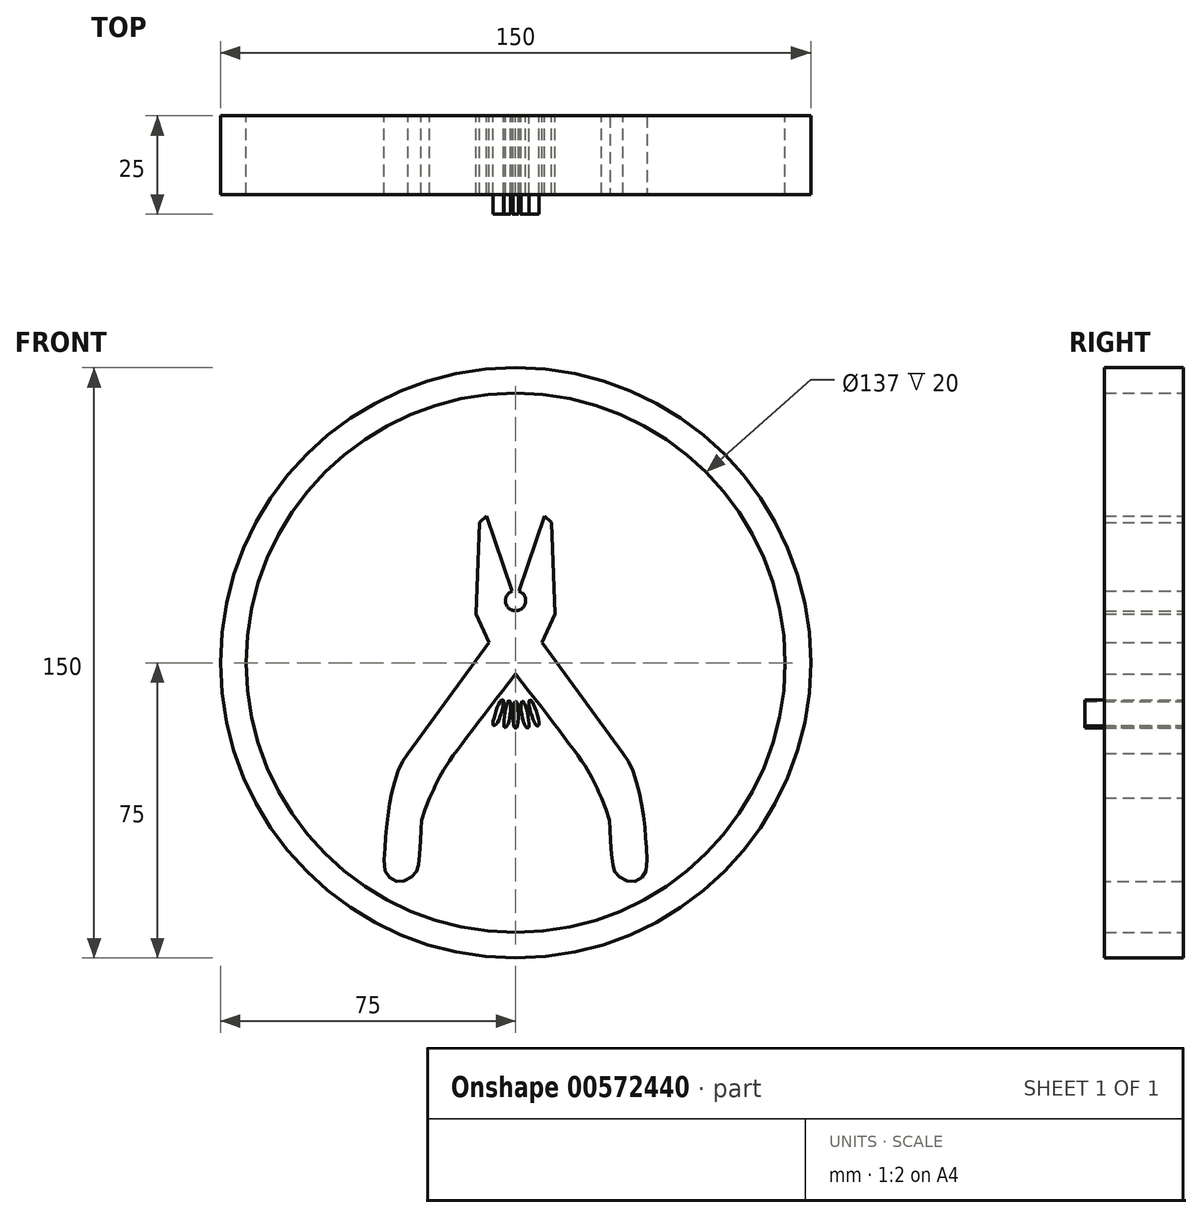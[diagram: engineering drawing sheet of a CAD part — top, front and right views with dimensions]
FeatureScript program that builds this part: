
annotation { "Feature Type Name" : "Feature", "Feature Type Description" : "" }
export const myFeature = defineFeature(function(context is Context, id is Id, definition is map)
    precondition{}
    {
        {
            var Q0;
            Q0=qCreatedBy(makeId("Front.planeOp"),FACE);
            var sketch = newSketch(context, id + "F0", { "sketchPlane" : qUnion([Q0])});
            skCircle(sketch, "E0", {"center": v(0, 0) * mm, "radius": 75 * mm});
            skCircle(sketch, "E1", {"center": v(0, 0) * mm, "radius": 68.5 * mm});
            skSolve(sketch);
        }
        {
            var Q0;
            Q0=qCreatedBy(makeId("Front.planeOp"),FACE);
            var sketch = newSketch(context, id + "F1", { "sketchPlane" : qUnion([Q0])});
            skLineSegment(sketch, "E2", {"start": v(-10, 12.39) * mm, "end": v(-9.1, 35.71) * mm});
            skLineSegment(sketch, "E3", {"start": v(-7.34, 37.33) * mm, "end": v(-9.1, 35.71) * mm});
            skLineSegment(sketch, "E4", {"start": v(-0.85, 18.26) * mm, "end": v(-7.34, 37.33) * mm});
            skLineSegment(sketch, "E5", {"start": v(0, -66.58) * mm, "end": v(0, 74.82) * mm});
            skLineSegment(sketch, "E6.MirrorCS", {"start": v(10, 12.39) * mm, "end": v(9.1, 35.71) * mm});
            skLineSegment(sketch, "E7.MirrorCS", {"start": v(7.34, 37.33) * mm, "end": v(9.1, 35.71) * mm});
            skLineSegment(sketch, "E8.MirrorCS", {"start": v(0.85, 18.26) * mm, "end": v(7.34, 37.33) * mm});
            skLineSegment(sketch, "E9", {"start": v(-6.7, 5.13) * mm, "end": v(-10, 12.39) * mm});
            skLineSegment(sketch, "E10", {"start": v(-6.7, 5.13) * mm, "end": v(-27.27, -22.98) * mm});
            skFitSpline(sketch, "E11", {"points": [v(-27.27, -22.98) * mm, v(-29.52, -26.66) * mm, v(-31.19, -31.98) * mm, v(-32.18, -37) * mm, v(-32.9, -42.7) * mm, v(-33.2, -47.05) * mm, v(-33.15, -52.71) * mm, v(-31.74, -54.8) * mm, v(-29.23, -55.6) * mm, v(-26.69, -54.58) * mm, v(-25.03, -52.76) * mm, v(-24.62, -50.5) * mm, v(-24.04, -43.94) * mm, v(-23.84, -39.86) * mm, v(-21.83, -34.33) * mm], "startDerivative": vector(-32.83, -46.76) * mm, "endDerivative": vector(25.22, 69.7) * mm});
            skFitSpline(sketch, "E12", {"points": [v(-21.83, -34.33) * mm, v(-20.19, -30.76) * mm, v(-17.28, -25.65) * mm, v(0, -2.87) * mm], "startDerivative": vector(9.4, 17.1) * mm, "endDerivative": vector(38.2, 48.97) * mm});
            skLineSegment(sketch, "E13.MirrorCS", {"start": v(6.7, 5.13) * mm, "end": v(27.27, -22.98) * mm});
            skFitSpline(sketch, "E14.MirrorCS", {"points": [v(27.27, -22.98) * mm, v(29.52, -26.66) * mm, v(31.19, -31.98) * mm, v(32.18, -37) * mm, v(32.9, -42.7) * mm, v(33.2, -47.05) * mm, v(33.15, -52.71) * mm, v(31.74, -54.8) * mm, v(29.23, -55.6) * mm, v(26.69, -54.58) * mm, v(25.03, -52.76) * mm, v(24.62, -50.5) * mm, v(24.04, -43.94) * mm, v(23.84, -39.86) * mm, v(21.83, -34.33) * mm], "startDerivative": vector(32.83, -46.76) * mm, "endDerivative": vector(-25.22, 69.7) * mm});
            skFitSpline(sketch, "E15.MirrorCS", {"points": [v(21.83, -34.33) * mm, v(20.19, -30.76) * mm, v(17.28, -25.65) * mm, v(0, -2.87) * mm], "startDerivative": vector(-9.4, 17.1) * mm, "endDerivative": vector(-38.2, 48.97) * mm});
            skLineSegment(sketch, "E16.MirrorCS", {"start": v(6.7, 5.13) * mm, "end": v(10, 12.39) * mm});
            skArc(sketch, "E17", {"start": v(-0.85, 18.26) * mm, "mid": v(0, 13.25) * mm, "end": v(0.85, 18.26) * mm});
            skSolve(sketch);
        }
        {
            var Q0;
            Q0=qCreatedBy(makeId("Front.planeOp"),FACE);
            var sketch = newSketch(context, id + "F2", { "sketchPlane" : qUnion([Q0])});
            skFitSpline(sketch, "E18", {"points": [v(-3.98, -9.96) * mm, v(-5.72, -15.04) * mm, v(-5.64, -15.82) * mm, v(-4.86, -15.53) * mm, v(-3.06, -10.2) * mm, v(-3.2, -9.44) * mm, v(-3.98, -9.96) * mm]});
            skFitSpline(sketch, "E19", {"points": [v(-2.14, -10.22) * mm, v(-2.96, -15.58) * mm, v(-2.8, -16.37) * mm, v(-2.1, -15.93) * mm, v(-1.26, -10.36) * mm, v(-1.56, -9.7) * mm, v(-2.14, -10.22) * mm]});
            skFitSpline(sketch, "E20", {"points": [v(-0.44, -10.44) * mm, v(-0.48, -15.9) * mm, v(0, -16.58) * mm, v(0.5, -15.94) * mm, v(0.44, -10.41) * mm, v(0, -9.83) * mm, v(-0.44, -10.44) * mm]});
            skFitSpline(sketch, "E21", {"points": [v(1.37, -10.63) * mm, v(2.36, -15.88) * mm, v(3.04, -16.5) * mm, v(3.4, -15.74) * mm, v(2.3, -10.35) * mm, v(1.75, -9.75) * mm, v(1.37, -10.63) * mm]});
            skFitSpline(sketch, "E22", {"points": [v(3.37, -10.2) * mm, v(4.87, -15.34) * mm, v(5.6, -16.02) * mm, v(5.92, -15.28) * mm, v(4.2, -9.9) * mm, v(3.57, -9.45) * mm, v(3.37, -10.2) * mm]});
            skFitSpline(sketch, "E23", {"points": [v(-13.47, -4.13) * mm, v(-16.08, -2.4) * mm, v(-17.3, -1.42) * mm, v(-20, -0.93) * mm, v(-21.37, -0.85) * mm, v(-21.77, -1.8) * mm, v(-21.82, -3.16) * mm, v(-21.65, -5.17) * mm, v(-21.56, -6.43) * mm, v(-21.68, -7.67) * mm, v(-21.77, -9.29) * mm, v(-21.96, -10.7) * mm, v(-22.66, -12.22) * mm, v(-23.33, -13.71) * mm, v(-24.22, -14) * mm, v(-25.5, -13.92) * mm, v(-27.2, -13.31) * mm, v(-28.1, -12.43) * mm, v(-29.04, -11.33) * mm, v(-30.5, -9.22) * mm, v(-30.99, -6.9) * mm, v(-31.16, -4.4) * mm, v(-31.16, -1.77) * mm, v(-31, 0.4) * mm], "startDerivative": vector(-48.66, 28.91) * mm, "endDerivative": vector(-3.44, 5.53) * mm});
            skFitSpline(sketch, "E24", {"points": [v(-31, 0.4) * mm, v(-30.88, 2.85) * mm, v(-30.32, 9) * mm, v(-29.28, 13.1) * mm, v(-26.86, 21.89) * mm, v(-24.96, 27.1) * mm, v(-22.12, 34.55) * mm, v(-19.6, 41) * mm, v(-17.58, 45.38) * mm, v(-15.62, 49.61) * mm, v(-14, 53.95) * mm, v(-14.22, 54.45) * mm, v(-14.94, 54.43) * mm, v(-16, 53.95) * mm, v(-17.36, 53.2) * mm, v(-18.07, 52.68) * mm, v(-18.67, 51.88) * mm, v(-19.18, 51.15) * mm, v(-19.32, 49.73) * mm, v(-19.55, 48.7) * mm, v(-19.8, 48.07) * mm, v(-20.3, 47.76) * mm, v(-20.59, 48.4) * mm, v(-20.92, 48.56) * mm, v(-21.2, 48.46) * mm, v(-21.37, 48.26) * mm, v(-21.53, 47.56) * mm, v(-21.99, 46.7) * mm, v(-22.33, 45) * mm, v(-22.33, 43.87) * mm, v(-22.28, 43.09) * mm, v(-22.72, 42.65) * mm, v(-23.3, 42.8) * mm, v(-23.45, 44.01) * mm, v(-23.74, 45) * mm, v(-24.48, 44.84) * mm, v(-24.66, 44.23) * mm, v(-25.07, 42.62) * mm, v(-25.6, 40.8) * mm, v(-25.74, 38.94) * mm, v(-25.42, 37) * mm, v(-25.02, 36.15) * mm, v(-25.23, 35.7) * mm, v(-25.98, 35.8) * mm, v(-26.35, 36.68) * mm, v(-26.59, 37.4) * mm, v(-26.72, 38.17) * mm, v(-26.8, 38.62) * mm, v(-26.83, 39.13) * mm, v(-27.33, 39.4) * mm, v(-27.9, 39.13) * mm, v(-28.1, 38.57) * mm, v(-28.61, 37.48) * mm, v(-28.9, 36.5) * mm, v(-29.28, 35.75) * mm, v(-29.52, 34.82) * mm, v(-29.96, 32.65) * mm, v(-29.8, 30.62) * mm, v(-29.29, 28.77) * mm, v(-29.83, 28.07) * mm, v(-30.87, 28.88) * mm, v(-31.49, 29.8) * mm, v(-32.2, 30.88) * mm, v(-32.48, 31.53) * mm, v(-32.96, 32.21) * mm, v(-33.07, 32.21) * mm, v(-33.22, 32.13) * mm, v(-33.4, 31.87) * mm, v(-33.92, 30.73) * mm, v(-33.95, 30.1) * mm, v(-34.05, 28.97) * mm, v(-34.11, 28.61) * mm, v(-34.05, 27.97) * mm, v(-34, 27.37) * mm, v(-34, 26.87) * mm, v(-33.95, 26.48) * mm, v(-33.85, 24.34) * mm, v(-33.58, 23.12) * mm, v(-33.12, 21.52) * mm, v(-32.86, 20.69) * mm, v(-32.66, 20.29) * mm, v(-32.82, 19.9) * mm, v(-33.4, 20.08) * mm, v(-34, 20.65) * mm, v(-34.76, 21.37) * mm, v(-35.55, 22.12) * mm, v(-36, 22.75) * mm, v(-36.45, 23.23) * mm, v(-36.86, 23.77) * mm, v(-37.3, 24.06) * mm, v(-37.56, 23.67) * mm, v(-37.68, 22.87) * mm, v(-37.66, 21.9) * mm, v(-37.72, 21.41) * mm, v(-37.68, 20.67) * mm, v(-37.64, 19.98) * mm, v(-37.62, 19.36) * mm, v(-37.62, 18.35) * mm, v(-37.62, 17.66) * mm, v(-37.56, 17.18) * mm, v(-37.56, 16.67) * mm, v(-37.4, 15.06) * mm, v(-36.94, 13.86) * mm, v(-36.32, 12.7) * mm, v(-35.62, 11.78) * mm, v(-34.9, 11.12) * mm, v(-34.83, 10.45) * mm, v(-35, 9.92) * mm, v(-35.58, 10.35) * mm, v(-38.88, 13.71) * mm, v(-40.64, 15.4) * mm, v(-41.72, 16.36) * mm, v(-41.98, 15.88) * mm, v(-41.88, 14.74) * mm, v(-41.79, 14) * mm, v(-41.69, 13.44) * mm, v(-41.62, 12.9) * mm, v(-41.55, 12.22) * mm, v(-41.3, 11.5) * mm, v(-41, 10.68) * mm, v(-40.65, 9.92) * mm, v(-40.33, 9.06) * mm, v(-40, 7.98) * mm, v(-39.44, 7.18) * mm, v(-38.62, 6.32) * mm, v(-39.13, 5.74) * mm, v(-40.38, 6.4) * mm, v(-41.58, 7.16) * mm, v(-43.16, 8.23) * mm, v(-45.26, 9.75) * mm, v(-45.7, 10.06) * mm, v(-46, 10.08) * mm, v(-46.3, 9.93) * mm, v(-46.4, 9.5) * mm, v(-46.3, 8.79) * mm, v(-46.28, 7.94) * mm, v(-46.06, 7.05) * mm, v(-45.57, 6.1) * mm, v(-44.97, 5.11) * mm, v(-43.87, 3.6) * mm, v(-42.7, 2.08) * mm, v(-41.65, 1.06) * mm, v(-41.12, 0.63) * mm, v(-40.92, 0.4) * mm, v(-41.2, 0.2) * mm, v(-42.06, 0.25) * mm, v(-42.78, 0.4) * mm, v(-43.47, 0.66) * mm, v(-44.3, 0.93) * mm, v(-45.62, 1.28) * mm, v(-46.58, 1.31) * mm, v(-46.78, 1.16) * mm, v(-46.83, 0.98) * mm, v(-46.83, 0.76) * mm, v(-46.63, -0.18) * mm, v(-46.13, -0.96) * mm, v(-45.62, -1.77) * mm, v(-45.12, -2.43) * mm, v(-44.59, -3) * mm, v(-43.61, -4.04) * mm, v(-42.82, -4.7) * mm, v(-42.4, -5) * mm, v(-42.2, -5.16) * mm, v(-42.12, -5.35) * mm, v(-42.34, -5.47) * mm, v(-42.85, -5.51) * mm, v(-44.87, -5.47) * mm, v(-46.1, -5.5) * mm, v(-47.24, -5.43) * mm, v(-47.54, -5.7) * mm, v(-47.52, -6.22) * mm, v(-47.09, -6.74) * mm, v(-46.59, -7.39) * mm, v(-46, -8.02) * mm, v(-45.2, -8.79) * mm, v(-44.62, -9.29) * mm, v(-44.05, -9.9) * mm, v(-43.24, -10.52) * mm, v(-42.54, -10.99) * mm, v(-41.6, -11.64) * mm, v(-40.78, -12.07) * mm, v(-39.95, -12.39) * mm, v(-38.98, -12.9) * mm, v(-38.42, -13.04) * mm, v(-38.42, -13.21) * mm, v(-38.55, -13.28) * mm, v(-39.17, -13.34) * mm, v(-40.6, -13.47) * mm, v(-41.67, -13.79) * mm, v(-42.3, -13.98) * mm, v(-43.1, -14.4) * mm, v(-43.87, -14.63) * mm, v(-44.51, -14.92) * mm, v(-44.54, -15.21) * mm, v(-44.25, -15.36) * mm, v(-43.78, -15.68) * mm, v(-42.87, -16.06) * mm, v(-41.26, -16.65) * mm, v(-39.53, -16.98) * mm, v(-37.63, -17.1) * mm, v(-35.74, -17.3) * mm, v(-34.13, -17.3) * mm, v(-33.04, -17.3) * mm, v(-32.82, -17.4) * mm, v(-32.9, -17.62) * mm, v(-33.19, -17.69) * mm, v(-33.96, -17.88) * mm, v(-34.89, -18.03) * mm, v(-36.08, -18.25) * mm, v(-36.78, -18.25) * mm, v(-37.83, -18.47) * mm, v(-38.77, -18.76) * mm, v(-40.11, -18.93) * mm, v(-41, -19.05) * mm, v(-42.15, -19.2) * mm, v(-42.9, -19.39) * mm, v(-43.05, -19.8) * mm, v(-42.88, -20.21) * mm, v(-42.54, -20.7) * mm, v(-41.81, -21.04) * mm, v(-41.1, -21.33) * mm, v(-39.94, -21.6) * mm, v(-38.8, -21.84) * mm, v(-37.68, -22.16) * mm, v(-36.44, -22.04) * mm, v(-35.37, -22.08) * mm, v(-33.8, -22.06) * mm, v(-32.94, -21.99) * mm, v(-31.73, -21.87) * mm, v(-30.54, -21.9) * mm, v(-29.42, -21.87) * mm, v(-28.55, -21.87) * mm, v(-27.99, -22.01) * mm, v(-27.56, -22.25) * mm, v(-27.35, -22.53) * mm, v(-27.53, -22.89) * mm, v(-27.78, -23.17) * mm, v(-28.1, -23.38) * mm, v(-28.58, -23.73) * mm, v(-29.4, -24.18) * mm, v(-30.22, -24.62) * mm, v(-30.87, -24.94) * mm, v(-31.37, -25.18) * mm, v(-31.85, -25.43) * mm, v(-31.92, -25.58) * mm, v(-31.82, -25.67) * mm, v(-31.64, -25.8) * mm, v(-31.36, -25.87) * mm, v(-31.16, -25.97) * mm, v(-30.33, -26.13) * mm, v(-29.84, -26.26) * mm, v(-29.54, -26.44) * mm, v(-29.4, -26.48) * mm, v(-29.4, -26.48) * mm], "startDerivative": vector(14.67, 321.67) * mm, "endDerivative": vector(0.41, 1.71) * mm});
            skFitSpline(sketch, "E25.MirrorCS", {"points": [v(31, 0.4) * mm, v(30.88, 2.85) * mm, v(30.32, 9) * mm, v(29.28, 13.1) * mm, v(26.86, 21.89) * mm, v(24.96, 27.1) * mm, v(22.12, 34.55) * mm, v(19.6, 41) * mm, v(17.58, 45.38) * mm, v(15.62, 49.61) * mm, v(14, 53.95) * mm, v(14.22, 54.45) * mm, v(14.94, 54.43) * mm, v(16, 53.95) * mm, v(17.36, 53.2) * mm, v(18.07, 52.68) * mm, v(18.67, 51.88) * mm, v(19.18, 51.15) * mm, v(19.32, 49.73) * mm, v(19.55, 48.7) * mm, v(19.8, 48.07) * mm, v(20.3, 47.76) * mm, v(20.59, 48.4) * mm, v(20.92, 48.56) * mm, v(21.2, 48.46) * mm, v(21.37, 48.26) * mm, v(21.53, 47.56) * mm, v(21.99, 46.7) * mm, v(22.33, 45) * mm, v(22.33, 43.87) * mm, v(22.28, 43.09) * mm, v(22.72, 42.65) * mm, v(23.3, 42.8) * mm, v(23.45, 44.01) * mm, v(23.74, 45) * mm, v(24.48, 44.84) * mm, v(24.66, 44.23) * mm, v(25.07, 42.62) * mm, v(25.6, 40.8) * mm, v(25.74, 38.94) * mm, v(25.42, 37) * mm, v(25.02, 36.15) * mm, v(25.23, 35.7) * mm, v(25.98, 35.8) * mm, v(26.35, 36.68) * mm, v(26.59, 37.4) * mm, v(26.72, 38.17) * mm, v(26.8, 38.62) * mm, v(26.83, 39.13) * mm, v(27.33, 39.4) * mm, v(27.9, 39.13) * mm, v(28.1, 38.57) * mm, v(28.61, 37.48) * mm, v(28.9, 36.5) * mm, v(29.28, 35.75) * mm, v(29.52, 34.82) * mm, v(29.96, 32.65) * mm, v(29.8, 30.62) * mm, v(29.29, 28.77) * mm, v(29.83, 28.07) * mm, v(30.87, 28.88) * mm, v(31.49, 29.8) * mm, v(32.2, 30.88) * mm, v(32.48, 31.53) * mm, v(32.96, 32.21) * mm, v(33.07, 32.21) * mm, v(33.22, 32.13) * mm, v(33.4, 31.87) * mm, v(33.92, 30.73) * mm, v(33.95, 30.1) * mm, v(34.05, 28.97) * mm, v(34.11, 28.61) * mm, v(34.05, 27.97) * mm, v(34, 27.37) * mm, v(34, 26.87) * mm, v(33.95, 26.48) * mm, v(33.85, 24.34) * mm, v(33.58, 23.12) * mm, v(33.12, 21.52) * mm, v(32.86, 20.69) * mm, v(32.66, 20.29) * mm, v(32.82, 19.9) * mm, v(33.4, 20.08) * mm, v(34, 20.65) * mm, v(34.76, 21.37) * mm, v(35.55, 22.12) * mm, v(36, 22.75) * mm, v(36.45, 23.23) * mm, v(36.86, 23.77) * mm, v(37.3, 24.06) * mm, v(37.56, 23.67) * mm, v(37.68, 22.87) * mm, v(37.66, 21.9) * mm, v(37.72, 21.41) * mm, v(37.68, 20.67) * mm, v(37.64, 19.98) * mm, v(37.62, 19.36) * mm, v(37.62, 18.35) * mm, v(37.62, 17.66) * mm, v(37.56, 17.18) * mm, v(37.56, 16.67) * mm, v(37.4, 15.06) * mm, v(36.94, 13.86) * mm, v(36.32, 12.7) * mm, v(35.62, 11.78) * mm, v(34.9, 11.12) * mm, v(34.83, 10.45) * mm, v(35, 9.92) * mm, v(35.58, 10.35) * mm, v(38.88, 13.71) * mm, v(40.64, 15.4) * mm, v(41.72, 16.36) * mm, v(41.98, 15.88) * mm, v(41.88, 14.74) * mm, v(41.79, 14) * mm, v(41.69, 13.44) * mm, v(41.62, 12.9) * mm, v(41.55, 12.22) * mm, v(41.3, 11.5) * mm, v(41, 10.68) * mm, v(40.65, 9.92) * mm, v(40.33, 9.06) * mm, v(40, 7.98) * mm, v(39.44, 7.18) * mm, v(38.62, 6.32) * mm, v(39.13, 5.74) * mm, v(40.38, 6.4) * mm, v(41.58, 7.16) * mm, v(43.16, 8.23) * mm, v(45.26, 9.75) * mm, v(45.7, 10.06) * mm, v(46, 10.08) * mm, v(46.3, 9.93) * mm, v(46.4, 9.5) * mm, v(46.3, 8.79) * mm, v(46.28, 7.94) * mm, v(46.06, 7.05) * mm, v(45.57, 6.1) * mm, v(44.97, 5.11) * mm, v(43.87, 3.6) * mm, v(42.7, 2.08) * mm, v(41.65, 1.06) * mm, v(41.12, 0.63) * mm, v(40.92, 0.4) * mm, v(41.2, 0.2) * mm, v(42.06, 0.25) * mm, v(42.78, 0.4) * mm, v(43.47, 0.66) * mm, v(44.3, 0.93) * mm, v(45.62, 1.28) * mm, v(46.58, 1.31) * mm, v(46.78, 1.16) * mm, v(46.83, 0.98) * mm, v(46.83, 0.76) * mm, v(46.63, -0.18) * mm, v(46.13, -0.96) * mm, v(45.62, -1.77) * mm, v(45.12, -2.43) * mm, v(44.59, -3) * mm, v(43.61, -4.04) * mm, v(42.82, -4.7) * mm, v(42.4, -5) * mm, v(42.2, -5.16) * mm, v(42.12, -5.35) * mm, v(42.34, -5.47) * mm, v(42.85, -5.51) * mm, v(44.87, -5.47) * mm, v(46.1, -5.5) * mm, v(47.24, -5.43) * mm, v(47.54, -5.7) * mm, v(47.52, -6.22) * mm, v(47.09, -6.74) * mm, v(46.59, -7.39) * mm, v(46, -8.02) * mm, v(45.2, -8.79) * mm, v(44.62, -9.29) * mm, v(44.05, -9.9) * mm, v(43.24, -10.52) * mm, v(42.54, -10.99) * mm, v(41.6, -11.64) * mm, v(40.78, -12.07) * mm, v(39.95, -12.39) * mm, v(38.98, -12.9) * mm, v(38.42, -13.04) * mm, v(38.42, -13.21) * mm, v(38.55, -13.28) * mm, v(39.17, -13.34) * mm, v(40.6, -13.47) * mm, v(41.67, -13.79) * mm, v(42.3, -13.98) * mm, v(43.1, -14.4) * mm, v(43.87, -14.63) * mm, v(44.51, -14.92) * mm, v(44.54, -15.21) * mm, v(44.25, -15.36) * mm, v(43.78, -15.68) * mm, v(42.87, -16.06) * mm, v(41.26, -16.65) * mm, v(39.53, -16.98) * mm, v(37.63, -17.1) * mm, v(35.74, -17.3) * mm, v(34.13, -17.3) * mm, v(33.04, -17.3) * mm, v(32.82, -17.4) * mm, v(32.9, -17.62) * mm, v(33.19, -17.69) * mm, v(33.96, -17.88) * mm, v(34.89, -18.03) * mm, v(36.08, -18.25) * mm, v(36.78, -18.25) * mm, v(37.83, -18.47) * mm, v(38.77, -18.76) * mm, v(40.11, -18.93) * mm, v(41, -19.05) * mm, v(42.15, -19.2) * mm, v(42.9, -19.39) * mm, v(43.05, -19.8) * mm, v(42.88, -20.21) * mm, v(42.54, -20.7) * mm, v(41.81, -21.04) * mm, v(41.1, -21.33) * mm, v(39.94, -21.6) * mm, v(38.8, -21.84) * mm, v(37.68, -22.16) * mm, v(36.44, -22.04) * mm, v(35.37, -22.08) * mm, v(33.8, -22.06) * mm, v(32.94, -21.99) * mm, v(31.73, -21.87) * mm, v(30.54, -21.9) * mm, v(29.42, -21.87) * mm, v(28.55, -21.87) * mm, v(27.99, -22.01) * mm, v(27.56, -22.25) * mm, v(27.35, -22.53) * mm, v(27.53, -22.89) * mm, v(27.78, -23.17) * mm, v(28.1, -23.38) * mm, v(28.58, -23.73) * mm, v(29.4, -24.18) * mm, v(30.22, -24.62) * mm, v(30.87, -24.94) * mm, v(31.37, -25.18) * mm, v(31.85, -25.43) * mm, v(31.92, -25.58) * mm, v(31.82, -25.67) * mm, v(31.64, -25.8) * mm, v(31.36, -25.87) * mm, v(31.16, -25.97) * mm, v(30.33, -26.13) * mm, v(29.84, -26.26) * mm, v(29.54, -26.44) * mm, v(29.4, -26.48) * mm, v(29.4, -26.48) * mm], "startDerivative": vector(-14.67, 321.67) * mm, "endDerivative": vector(-0.41, 1.71) * mm});
            skFitSpline(sketch, "E26.MirrorCS", {"points": [v(13.47, -4.13) * mm, v(16.08, -2.4) * mm, v(17.3, -1.42) * mm, v(20, -0.93) * mm, v(21.37, -0.85) * mm, v(21.77, -1.8) * mm, v(21.82, -3.16) * mm, v(21.65, -5.17) * mm, v(21.56, -6.43) * mm, v(21.68, -7.67) * mm, v(21.77, -9.29) * mm, v(21.96, -10.7) * mm, v(22.66, -12.22) * mm, v(23.33, -13.71) * mm, v(24.22, -14) * mm, v(25.5, -13.92) * mm, v(27.2, -13.31) * mm, v(28.1, -12.43) * mm, v(29.04, -11.33) * mm, v(30.5, -9.22) * mm, v(30.99, -6.9) * mm, v(31.16, -4.4) * mm, v(31.16, -1.77) * mm, v(31, 0.4) * mm], "startDerivative": vector(48.66, 28.91) * mm, "endDerivative": vector(3.44, 5.53) * mm});
            skSolve(sketch);
        }
        {
            var Q0;
            Q0 = qSketchRegion(id + "F0", true);
            extrude(context, id + "F3", {"entities" : qUnion([Q0]), "depth" : 20 * mm, "offsetDistance" : 25 * mm});
        }
        {
            var Q0;
            Q0 = qSketchRegion(id + "F1", true);
            extrude(context, id + "F4", {"entities" : qUnion([Q0]), "depth" : 20 * mm, "offsetDistance" : 25 * mm});
        }
        {
            var Q0;
            Q0 = qSketchRegion(id + "F2", true);
            extrude(context, id + "F5", {"entities" : qUnion([Q0]), "depth" : 25 * mm, "offsetDistance" : 25 * mm});
        }
        {
            var Q0;
            Q0=sQuery(id+"F2.wireOp",EDGE,"E23");
            var Q1;
            Q1=sQuery(id+"F2.wireOp",EDGE,"E24");
            var Q2;
            Q2=sQuery(id+"F2.wireOp",EDGE,"E26.MirrorCS");
            var Q3;
            Q3=sQuery(id+"F2.wireOp",EDGE,"E25.MirrorCS");
            extrude(context, id + "F6", {"bodyType" : ToolBodyType.SURFACE, "surfaceEntities" : qUnion([Q0, Q1, Q2, Q3]), "depth" : 15 * mm, "offsetDistance" : 25 * mm});
        }
    });
